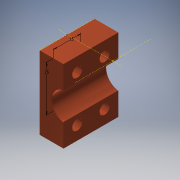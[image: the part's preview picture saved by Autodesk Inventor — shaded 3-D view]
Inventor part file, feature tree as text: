
AUTODESK INVENTOR PART (.ipt)
format: ipt  version: 2016 SP2 (Build 200236200, 236)  size: 472,576 bytes
history: native  units: mm
features: sketch x6, other x3, hole x2, plane x2, fillet x1
ambient origin geometry x8: Origin, YZ Plane, XZ Plane, XY Plane, X Axis, Y Axis, Z Axis, Center Point
bodies: Solid1 (feature_tree)
feature tree (14):
  other  "17-0028-0025.ipt"
  sketch  "Sketch1"  dims[d0=10.0mm d1=15.0mm d2=25.0mm]
  sketch  "Sketch2"  dims[d10=5.5mm d11=6.0mm d12=10.0mm d13=5.7mm d14=90.0deg d15=8.0mm d16=0.0mm d17=6.0mm]
  hole  "Hole3"  [1 undecoded]
  fillet  "Fillet1"  Radius=25.0mm
  sketch  "Sketch5"  dims[d20=-2.8mm]
  plane  "Work Plane1"
  sketch  "Sketch6"  dims[d21=12.4mm]
  plane  "Work Plane2"
  sketch  "Sketch7"  dims[d22=0.3mm]
  other  "Solid4::17-0028-0025.ipt"
  other  "TaggingFeature1"
  sketch  "Sketch4"  dims[d18=-5.5mm]
  hole  "Hole2"  [1 undecoded]
note: 2 required parameter values undecoded (feature->parameter linkage not recoverable at this tier; creation-order binding heuristic only, values carry confidence <= 0.55)
